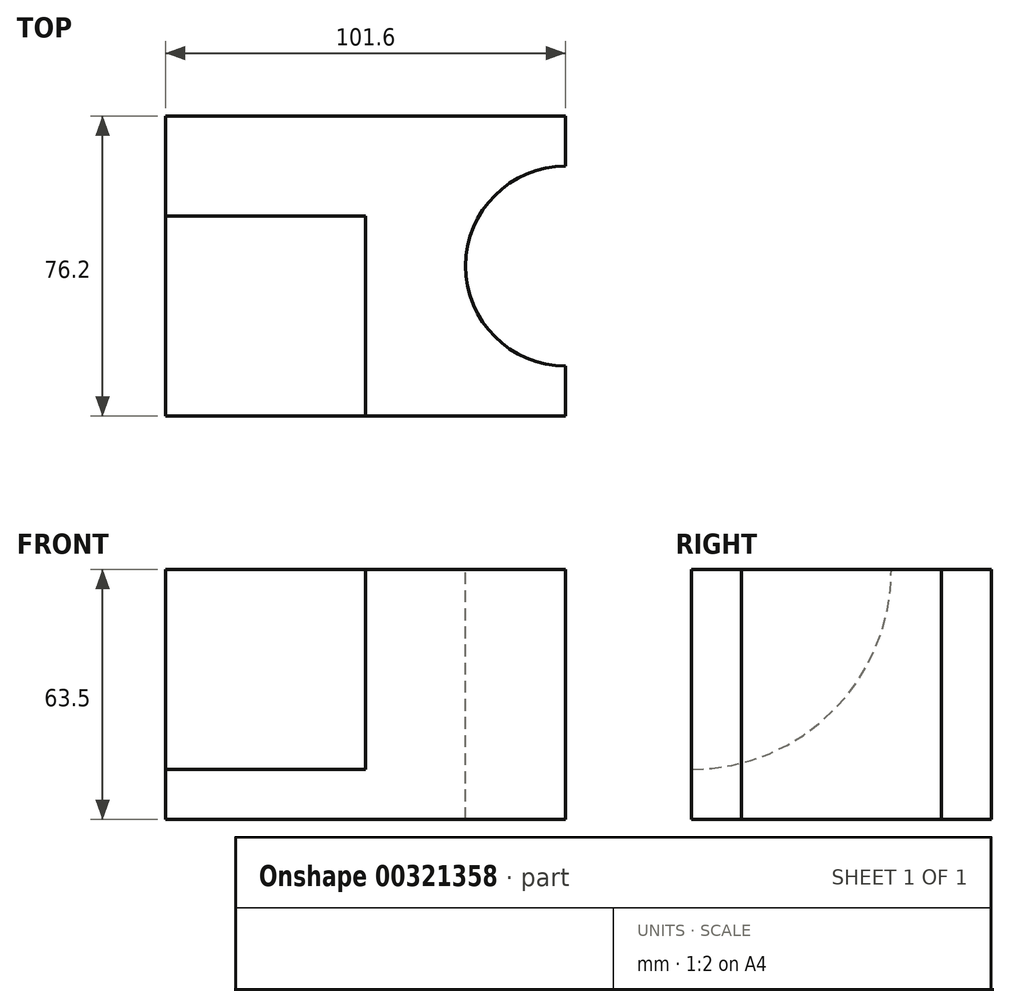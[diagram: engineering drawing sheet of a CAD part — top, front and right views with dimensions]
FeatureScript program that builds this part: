
annotation { "Feature Type Name" : "Feature", "Feature Type Description" : "" }
export const myFeature = defineFeature(function(context is Context, id is Id, definition is map)
    precondition{}
    {
        {
            var Q0;
            Q0=qCreatedBy(makeId("Front.planeOp"),FACE);
            var sketch = newSketch(context, id + "F0", { "sketchPlane" : qUnion([Q0])});
            skLineSegment(sketch, "E0.bottom", {"start": v(-51.52, 26.93) * mm, "end": v(50.08, 26.93) * mm});
            skLineSegment(sketch, "E0.top", {"start": v(-51.52, -36.57) * mm, "end": v(50.08, -36.57) * mm});
            skLineSegment(sketch, "E0.left", {"start": v(-51.52, 26.93) * mm, "end": v(-51.52, -36.57) * mm});
            skLineSegment(sketch, "E0.right", {"start": v(50.08, 26.93) * mm, "end": v(50.08, -36.57) * mm});
            skSolve(sketch);
        }
        {
            var Q0;
            Q0=makeQuery(id+"F0.imprint","IMPRINT",FACE,{"disambiguationData":[TD([[makeQuery(id+"F0.imprint","IMPRINT",EDGE,{"derivedFrom":sQuery(id+"F0.wireOp",EDGE,"E0.bottom")}),-1.0]])]});
            extrude(context, id + "F1", {"entities" : qUnion([Q0]), "depth" : 76.2 * mm});
        }
        {
            var Q0;
            Q0=makeQuery(id+"F1.opExtrude","SWEPT_FACE",FACE,{"disambiguationData":[OSD([sQuery(id+"F0.wireOp",EDGE,"E0.bottom")])]});
            var sketch = newSketch(context, id + "F2", { "sketchPlane" : qUnion([Q0])});
            skArc(sketch, "E1", {"start": v(50.08, -12.7) * mm, "mid": v(24.68, -38.1) * mm, "end": v(50.08, -63.5) * mm});
            skLineSegment(sketch, "E2", {"start": v(50.08, -12.7) * mm, "end": v(50.08, -63.5) * mm});
            skSolve(sketch);
        }
        {
            var Q0;
            Q0=makeQuery(id+"F2.imprint","IMPRINT",FACE,{"disambiguationData":[TD([[makeQuery(id+"F2.imprint","IMPRINT",EDGE,{"derivedFrom":sQuery(id+"F2.wireOp",EDGE,"E1")}),1.0]])]});
            extrude(context, id + "F3", {"entities" : qUnion([Q0]), "operationType" : NewBodyOperationType.REMOVE, "endBound" : BoundingType.THROUGH_ALL, "oppositeDirection" : true, "depth" : 25.4 * mm});
        }
        {
            var Q0;
            Q0=makeQuery(id+"F1.opExtrude","SWEPT_FACE",FACE,{"disambiguationData":[OSD([sQuery(id+"F0.wireOp",EDGE,"E0.left")])]});
            var sketch = newSketch(context, id + "F4", { "sketchPlane" : qUnion([Q0])});
            skArc(sketch, "E3", {"start": v(25.4, 26.93) * mm, "mid": v(40.28, -8.99) * mm, "end": v(76.2, -23.87) * mm});
            skLineSegment(sketch, "E4", {"start": v(25.4, 26.93) * mm, "end": v(76.2, 26.93) * mm});
            skLineSegment(sketch, "E5", {"start": v(76.2, 26.93) * mm, "end": v(76.2, -23.87) * mm});
            skSolve(sketch);
        }
        {
            var Q0;
            Q0 = qSketchRegion(id + "F4", true);
            extrude(context, id + "F5", {"entities" : qUnion([Q0]), "operationType" : NewBodyOperationType.REMOVE, "oppositeDirection" : true, "depth" : 50.8 * mm});
        }
    });
